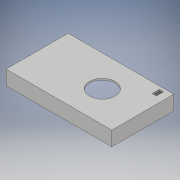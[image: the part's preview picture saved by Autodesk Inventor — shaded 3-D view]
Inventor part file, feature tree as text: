
AUTODESK INVENTOR PART (.ipt)
format: ipt  version: 2018 (Build 220112000, 112)  size: 194,560 bytes
history: native  units: mm
features: extrude x6, sketch x6
ambient origin geometry x8: Origin, YZ Plane, XZ Plane, XY Plane, X Axis, Y Axis, Z Axis, Center Point
bodies: Solid1 (feature_tree)
feature tree (12):
  extrude  "Extrusion1"  Depth=57.5mm
  extrude  "Extrusion2"  Depth=1.5mm
  extrude  "Extrusion3"  Depth=1.5mm TaperAngle=0.0deg
  extrude  "Extrusion4"  Depth=12.6mm TaperAngle=0.0deg
  extrude  "Extrusion5"  Depth=7.0mm
  extrude  "Extrusion6"  Depth=10.0mm
  sketch  "Sketch1"  dims[d0=100.0mm d1=57.5mm]
  sketch  "Sketch2"  dims[d2=1.5mm d3=25.0mm]
  sketch  "Sketch3"  dims[d4=38.0mm d5=1.5mm d6=0.0mm]
  sketch  "Sketch4"  dims[d7=1.5mm d8=12.6mm d9=0.0mm]
  sketch  "Sketch5"  dims[d10=3.0mm d11=7.0mm]
  sketch  "Sketch6"  dims[d12=4.0mm d13=10.0mm d14=12.6mm d15=0.0mm d16=9.0mm d18=27.5mm d19=12.5mm d20=12.6mm d21=49.0mm d22=38.5mm d23=12.6mm d24=0.0mm d25=3.0mm d26=3.0mm d27=3.0mm d28=3.0mm d31=3.75mm d32=3.75mm d33=3.75mm d34=2.75mm d35=2.75mm d36=2.75mm d37=3.75mm d39=2.75mm d40=12.6mm d41=0.0mm d42=6.0mm d43=6.0mm d44=6.0mm d45=6.0mm d46=6.0mm d47=6.0mm d48=10.6mm d49=0.0mm]
